# Revit family: FU_Chair_Sandler_Slim-1-3
name_source: partatom
category: Furniture
units: mm (PartAtom-declared; Revit-internal decimal feet)

## family parameters
Always vertical = Yes
Cut with Voids When Loaded = No
OmniClass Number = 23.40.20.00
OmniClass Title = General Furniture and Specialties
Render Appearance Source = Family Geometry
Room Calculation Point = No
Shared = No
Work Plane-Based = No

## types (1)
- Slim 1.3
    Default Elevation = 0 mm  [stored 0 ft]
    Depth = 510 mm  [stored 1.67323 ft]
    Description = Side chair on steel sled base. Fully upholstered with line detailing on chair back. Stacks 15 pieces on floor and 12 pieces on a trolley. MOQ 100 pieces
    Height = 840 mm  [stored 2.75591 ft]
    Manufacturer = Sandler
    Model = Slim 1.3
    URL = https://www.sandlerseating.com
    Width = 580 mm  [stored 1.90289 ft]

note: [stored X ft] marks values corroborated as IEEE doubles in the binary element streams (Revit-internal decimal feet)

## geometry (parser evidence)
native form markers: Sweep x10
no freeform markers — native parametric forms only
